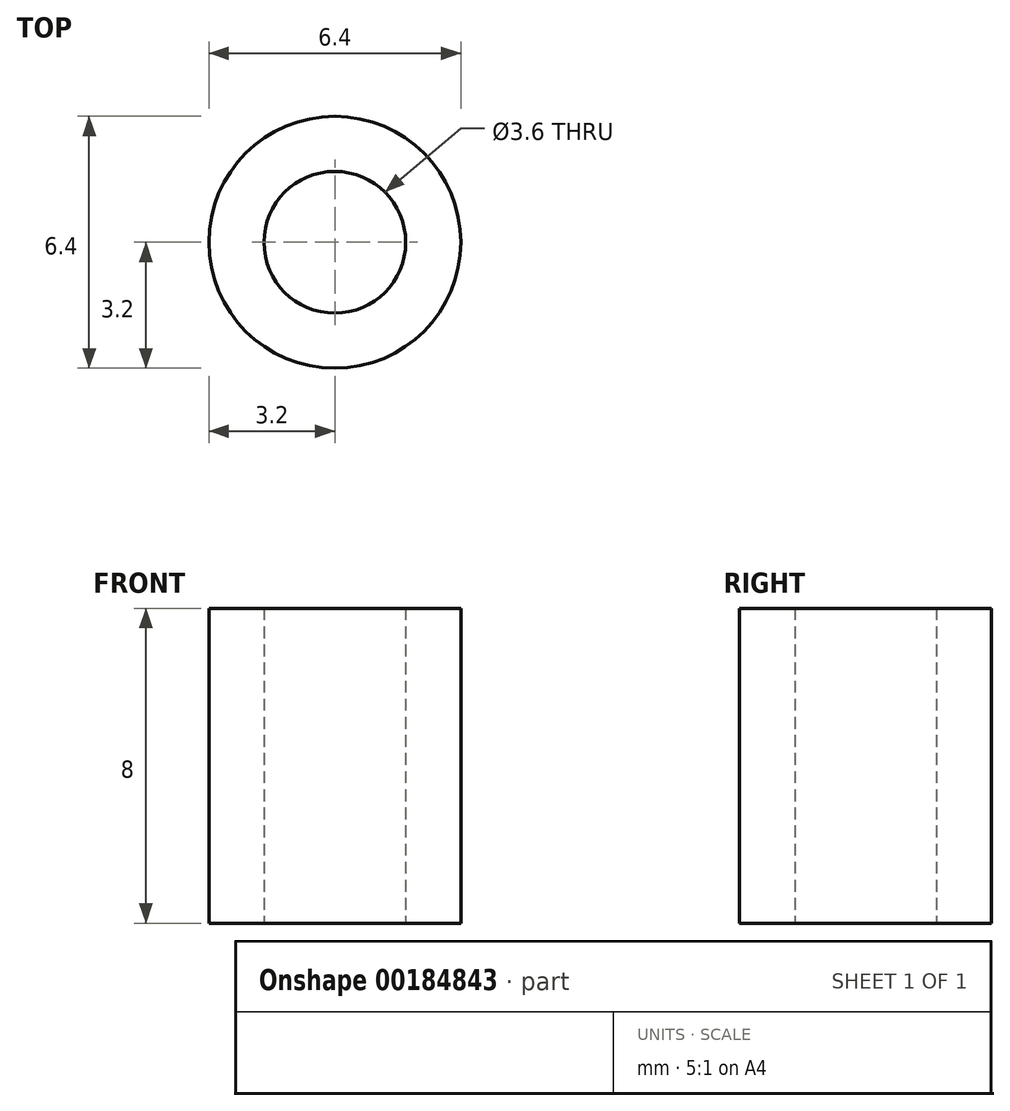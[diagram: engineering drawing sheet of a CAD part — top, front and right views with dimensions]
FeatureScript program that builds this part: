
annotation { "Feature Type Name" : "Feature", "Feature Type Description" : "" }
export const myFeature = defineFeature(function(context is Context, id is Id, definition is map)
    precondition{}
    {
        {
            var Q0;
            Q0=qCreatedBy(makeId("Top.planeOp"),FACE);
            var sketch = newSketch(context, id + "F0", { "sketchPlane" : qUnion([Q0])});
            skCircle(sketch, "E0", {"center": v(0, 0) * mm, "radius": 3.2 * mm});
            skCircle(sketch, "E1", {"center": v(0, 0) * mm, "radius": 1.8 * mm});
            skSolve(sketch);
        }
        {
            var Q0;
            Q0=makeQuery(id+"F0.imprint","IMPRINT",FACE,{"disambiguationData":[TD([[makeQuery(id+"F0.imprint","IMPRINT",EDGE,{"derivedFrom":sQuery(id+"F0.wireOp",EDGE,"E0")}),1.0]])]});
            extrude(context, id + "F1", {"entities" : qUnion([Q0]), "depth" : 8 * mm});
        }
    });
